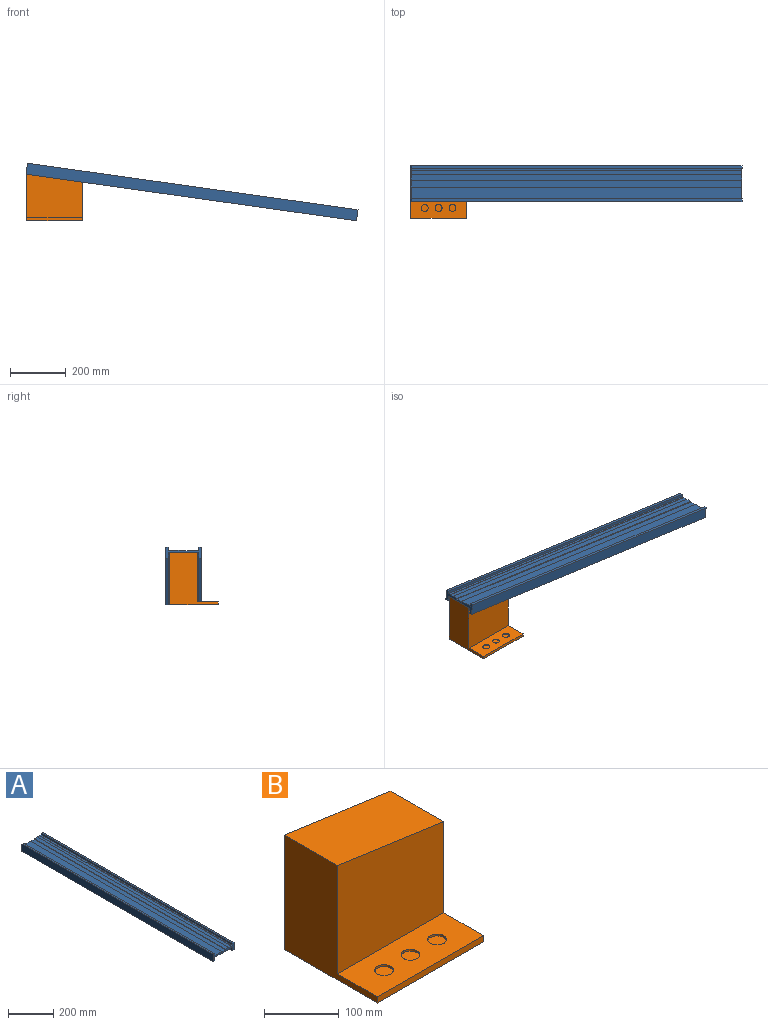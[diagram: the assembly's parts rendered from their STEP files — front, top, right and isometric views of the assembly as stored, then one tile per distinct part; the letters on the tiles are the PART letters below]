
ASSEMBLY  parts=2 mates=1
PART A: 22 faces, bbox 130x1200x40 mm
  f0: plane 1200x1mm, normal (-1,0,0), area 1200mm2, adj f15,f17,f18,f19
  f1: plane 1200x25mm, normal (0,0,1), area 30000mm2, adj f2,f16,f17,f19
  f2: plane 1200x3mm, normal (1,0,0), area 3600mm2, adj f1,f3,f17,f19
  f3: plane 1200x42.5mm, normal (0,0,1), area 51000mm2, adj f2,f4,f17,f19
  f4: plane 1200x10mm, normal (1,0,0), area 12000mm2, adj f3,f5,f17,f19
  f5: plane 1200x10mm, normal (0,0,1), area 12000mm2, adj f4,f6,f17,f19
  f6: plane 1200x40mm, normal (-1,0,0), area 48000mm2, adj f5,f7,f17,f19
  f7: plane 1200x10mm, normal (0,0,-1), area 12000mm2, adj f6,f8,f17,f19
  f8: plane 1200x20mm, normal (1,0,0), area 24000mm2, adj f7,f9,f17,f19
  f9: plane 1200x110mm, normal (0,0,-1), area 132000mm2, adj f8,f10,f17,f19
  f10: plane 1200x20mm, normal (-1,0,0), area 24000mm2, adj f9,f11,f17,f19
  f11: plane 1200x10mm, normal (0,0,-1), area 12000mm2, adj f10,f12,f17,f19
  f12: plane 1200x40mm, normal (1,0,0), area 48000mm2, adj f11,f13,f17,f19
  f13: plane 1200x10mm, normal (0,0,1), area 12000mm2, adj f12,f14,f17,f19
  f14: plane 1200x10mm, normal (-1,0,0), area 12000mm2, adj f13,f15,f17,f19
  f15: plane 1200x7.5mm, normal (0,0,1), area 9000mm2, adj f0,f14,f17,f19
  f16: plane 1200x3mm, normal (-1,0,0), area 3600mm2, adj f1,f17,f19,f20
  f17: plane 130x40mm, normal (0,1,0), area 1810mm2, adj f0,f1,f2,f3,f4,f5,f6,f7
  f18: plane 1200x15mm, normal (0,0,1), area 18000mm2, adj f0,f17,f19,f21
  f19: plane 130x40mm, normal (0,-1,0), area 1810mm2, adj f0,f1,f2,f3,f4,f5,f6,f7
  f20: plane 1200x20mm, normal (0,0,1), area 24000mm2, adj f16,f17,f19,f21
  f21: plane 1200x1mm, normal (1,0,0), area 1200mm2, adj f17,f18,f19,f20
PART B: 14 faces, bbox 200x175x186.8 mm
  f0: plane 25x25mm, normal (0,0,1), area 490.9mm2, adj f5
  f1: plane 25x25mm, normal (0,0,1), area 490.9mm2, adj f6
  f2: plane 200x186.81mm, normal (0,1,0), area 34551.8mm2, adj f3,f4,f8,f10
  f3: plane 200x100mm, normal (0.14,0,0.99), area 20196.6mm2, adj f2,f7,f8,f10
  f4: plane 200x175mm, normal (0,0,-1), area 35000mm2, adj f2,f8,f9,f10
  f5: cylinder r=12.5mm len=25mm, axis (0,0,-1), area 235.6mm2, adj f0,f11
  f6: cylinder r=12.5mm len=25mm, axis (0,0,-1), area 235.6mm2, adj f1,f11
  f7: plane 200x176.81mm, normal (0,-1,0), area 32551.8mm2, adj f3,f8,f10,f11
  f8: plane 186.81x175mm, normal (-1,0,0), area 19431.3mm2, adj f2,f3,f4,f7,f9,f11
  f9: plane 200x10mm, normal (0,-1,0), area 2000mm2, adj f4,f8,f10,f11
  f10: plane 175x158.71mm, normal (1,0,0), area 16620.5mm2, adj f2,f3,f4,f7,f9,f11
  f11: plane 200x75mm, normal (0,0,1), area 13527.4mm2, adj f5,f6,f7,f8,f9,f10,f13
  f12: plane 25x25mm, normal (0,0,1), area 490.9mm2, adj f13
  f13: cylinder r=12.5mm len=25mm, axis (0,0,-1), area 235.6mm2, adj f11,f12
PLACE A rot(axis=(0.07,0.07,1),90.3deg) t=(24.41,7.61,-1.94)mm
PLACE B t=(-569.75,57.61,-105.25)mm fixed
MATE fastened A.f9 <-> B.f3  axis (-0.14,0,-0.99) through (-569.75,7.61,81.56)mm
